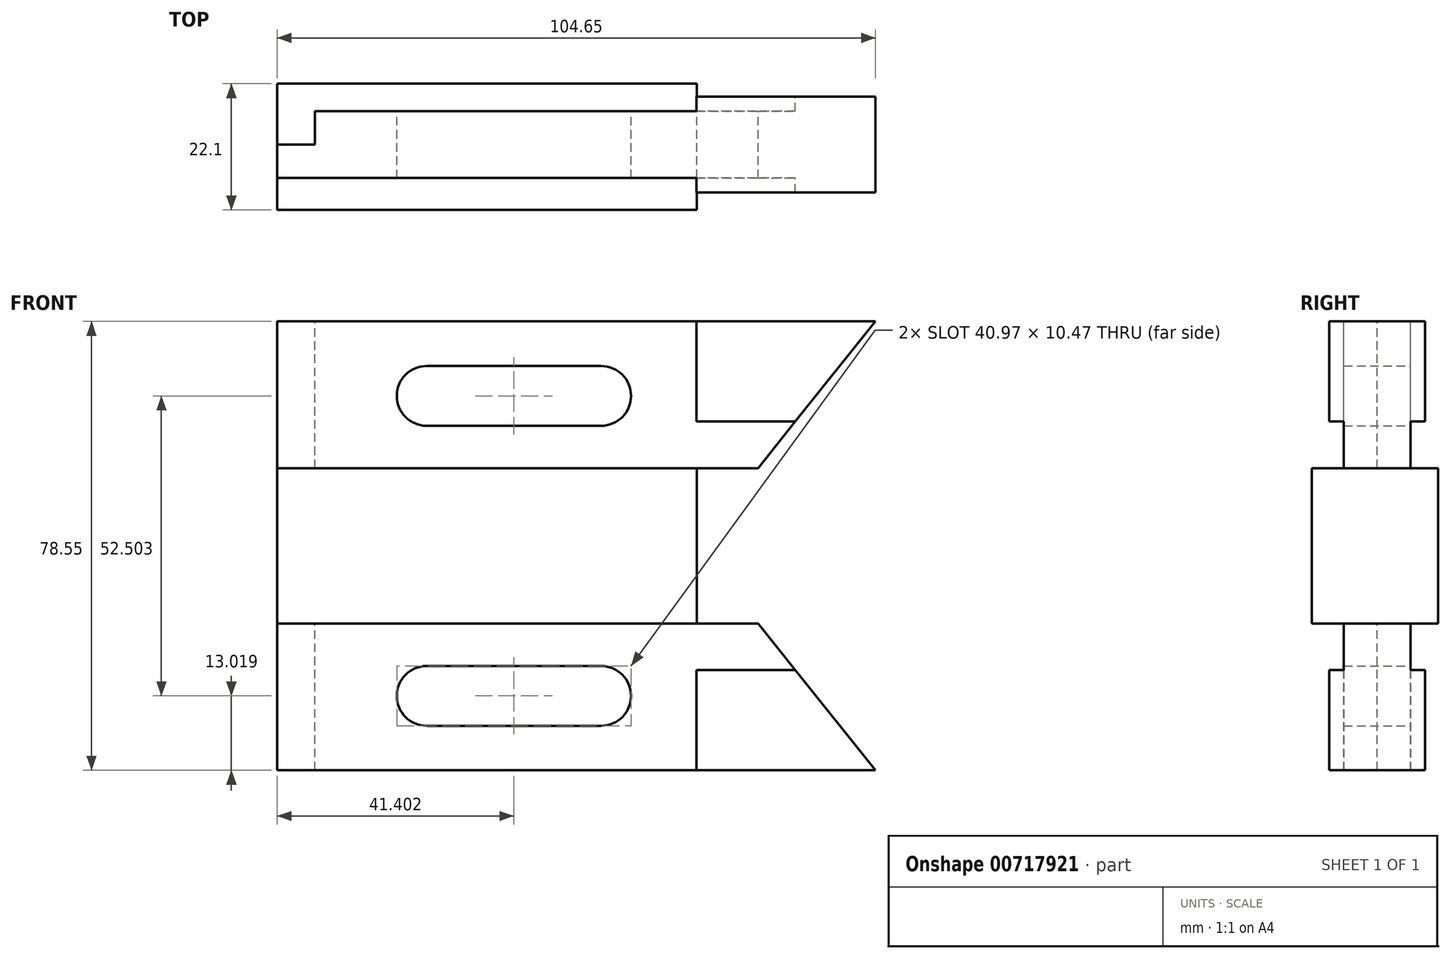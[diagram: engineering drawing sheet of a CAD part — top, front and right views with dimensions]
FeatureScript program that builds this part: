
annotation { "Feature Type Name" : "Feature", "Feature Type Description" : "" }
export const myFeature = defineFeature(function(context is Context, id is Id, definition is map)
    precondition{}
    {
        {
            var Q0;
            Q0=qCreatedBy(makeId("Front.planeOp"),FACE);
            var sketch = newSketch(context, id + "F0", { "sketchPlane" : qUnion([Q0])});
            skLineSegment(sketch, "E0", {"start": v(35.4, 0) * mm, "end": v(-38, 0) * mm});
            skLineSegment(sketch, "E1", {"start": v(-38, 10.01) * mm, "end": v(-38, 18.12) * mm});
            skLineSegment(sketch, "E2", {"start": v(-38, 0) * mm, "end": v(-38, 27.2) * mm});
            skLineSegment(sketch, "E3", {"start": v(-38, 27.2) * mm, "end": v(35.4, 27.2) * mm});
            skLineSegment(sketch, "E4", {"start": v(35.4, 27.2) * mm, "end": v(35.4, 0) * mm});
            skSolve(sketch);
        }
        {
            var Q0;
            {var subQ0=sQuery(id+"F0.wireOp",EDGE,"E0");Q0=makeQuery(id+"F0.imprint","IMPRINT",FACE,{"disambiguationData":[TD([[makeQuery(id+"F0.imprint","IMPRINT",EDGE,{"derivedFrom":subQ0}),-1.0]])]});}
            extrude(context, id + "F1", {"entities" : qUnion([Q0]), "depth" : 22.1 * mm, "offsetDistance" : 25.4 * mm});
        }
        {
            var Q0;
            Q0=qCreatedBy(makeId("Front.planeOp"),FACE);
            cPlane(context, id + "F2", {"entities" : qUnion([Q0]), "cplaneType" : CPlaneType.OFFSET, "offset" : 10.67 * mm, "width" : 152.4 * mm, "height" : 152.4 * mm});
        }
        {
            var Q0;
            Q0=qCreatedBy(id+"F2.planeOp",FACE);
            var sketch = newSketch(context, id + "F3", { "sketchPlane" : qUnion([Q0])});
            skLineSegment(sketch, "E5", {"start": v(-38, 27.2) * mm, "end": v(46.1, 27.2) * mm});
            skLineSegment(sketch, "E6", {"start": v(46.1, 27.2) * mm, "end": v(66.64, 52.87) * mm});
            skLineSegment(sketch, "E7", {"start": v(-38, 27.2) * mm, "end": v(-38, 52.87) * mm});
            skLineSegment(sketch, "E8", {"start": v(-38, 52.87) * mm, "end": v(66.64, 52.87) * mm});
            skLineSegment(sketch, "E9", {"start": v(-38, 0) * mm, "end": v(46.1, 0) * mm});
            skLineSegment(sketch, "E10", {"start": v(46.1, 0) * mm, "end": v(66.64, -25.68) * mm});
            skLineSegment(sketch, "E11", {"start": v(66.64, -25.68) * mm, "end": v(-38, -25.68) * mm});
            skLineSegment(sketch, "E12", {"start": v(-38, -25.68) * mm, "end": v(-38, 0) * mm});
            skLineSegment(sketch, "E13", {"start": v(-31.41, -25.68) * mm, "end": v(-31.41, 0) * mm});
            skLineSegment(sketch, "E14", {"start": v(-31.41, 0) * mm, "end": v(35.33, 0) * mm});
            skLineSegment(sketch, "E15", {"start": v(35.33, 0) * mm, "end": v(46.1, 0) * mm});
            skLineSegment(sketch, "E16", {"start": v(52.62, -8.15) * mm, "end": v(35.33, -8.15) * mm});
            skLineSegment(sketch, "E17", {"start": v(35.33, -8.15) * mm, "end": v(35.33, -25.68) * mm});
            skLineSegment(sketch, "E18", {"start": v(52.62, 35.34) * mm, "end": v(35.33, 35.34) * mm});
            skLineSegment(sketch, "E19", {"start": v(35.33, 35.34) * mm, "end": v(35.33, 52.87) * mm});
            skLineSegment(sketch, "E20", {"start": v(-31.41, 27.2) * mm, "end": v(-31.41, 52.87) * mm});
            skLineSegment(sketch, "E21", {"start": v(-11.86, -17.9) * mm, "end": v(18.64, -17.9) * mm});
            skArc(sketch, "E22", {"start": v(18.64, -17.9) * mm, "mid": v(23.88, -12.66) * mm, "end": v(18.64, -7.43) * mm});
            skLineSegment(sketch, "E23", {"start": v(18.64, -7.43) * mm, "end": v(-11.86, -7.43) * mm});
            skArc(sketch, "E24", {"start": v(-11.86, -7.43) * mm, "mid": v(-17.1, -12.66) * mm, "end": v(-11.86, -17.9) * mm});
            skLineSegment(sketch, "E25", {"start": v(18.64, 34.6) * mm, "end": v(-11.86, 34.6) * mm});
            skArc(sketch, "E26", {"start": v(18.64, 34.6) * mm, "mid": v(23.88, 39.84) * mm, "end": v(18.64, 45.08) * mm});
            skLineSegment(sketch, "E27", {"start": v(18.64, 45.08) * mm, "end": v(-11.86, 45.08) * mm});
            skArc(sketch, "E28", {"start": v(-11.86, 45.08) * mm, "mid": v(-17.1, 39.84) * mm, "end": v(-11.86, 34.6) * mm});
            skSolve(sketch);
        }
        {
            var Q0;
            {var subQ1=sQuery(id+"F3.wireOp",EDGE,"E13");Q0=makeQuery(id+"F3.imprint","IMPRINT",FACE,{"disambiguationData":[TD([[makeQuery(id+"F3.imprint","IMPRINT",EDGE,{"derivedFrom":subQ1}),-1.0]])]});}
            var Q1;
            {var subQ0=sQuery(id+"F3.wireOp",EDGE,"E18");Q1=makeQuery(id+"F3.imprint","IMPRINT",FACE,{"disambiguationData":[TD([[makeQuery(id+"F3.imprint","IMPRINT",EDGE,{"derivedFrom":subQ0}),1.0]])]});}
            extrude(context, id + "F4", {"entities" : qUnion([Q0, Q1]), "operationType" : NewBodyOperationType.ADD, "endBound" : BoundingType.SYMMETRIC, "depth" : 11.68 * mm, "offsetDistance" : 25.4 * mm});
        }
        {
            var Q0;
            {var subQ0=sQuery(id+"F3.wireOp",EDGE,"E16");Q0=makeQuery(id+"F3.imprint","IMPRINT",FACE,{"disambiguationData":[TD([[makeQuery(id+"F3.imprint","IMPRINT",EDGE,{"derivedFrom":subQ0}),1.0]])]});}
            var Q1;
            {var subQ0=sQuery(id+"F3.wireOp",EDGE,"E18");Q1=makeQuery(id+"F3.imprint","IMPRINT",FACE,{"disambiguationData":[TD([[makeQuery(id+"F3.imprint","IMPRINT",EDGE,{"derivedFrom":subQ0}),-1.0]])]});}
            extrude(context, id + "F5", {"entities" : qUnion([Q0, Q1]), "operationType" : NewBodyOperationType.ADD, "endBound" : BoundingType.SYMMETRIC, "depth" : 16.76 * mm, "offsetDistance" : 25.4 * mm});
        }
        {
            var Q0;
            {var subQ2=sQuery(id+"F3.wireOp",EDGE,"E12");Q0=makeQuery(id+"F3.imprint","IMPRINT",FACE,{"disambiguationData":[TD([[makeQuery(id+"F3.imprint","IMPRINT",EDGE,{"derivedFrom":subQ2}),-1.0]])]});}
            var Q1;
            Q1=makeQuery(id+"F4.opExtrude","CAP_FACE",FACE,{"disambiguationData":[OSD([sQuery(id+"F3.wireOp",EDGE,"E9"),sQuery(id+"F3.wireOp",EDGE,"E10"),sQuery(id+"F3.wireOp",EDGE,"E11"),sQuery(id+"F3.wireOp",EDGE,"E13"),sQuery(id+"F3.wireOp",EDGE,"E16"),sQuery(id+"F3.wireOp",EDGE,"E17"),sQuery(id+"F3.wireOp",EDGE,"E21"),sQuery(id+"F3.wireOp",EDGE,"E22"),sQuery(id+"F3.wireOp",EDGE,"E23"),sQuery(id+"F3.wireOp",EDGE,"E24")])],"isStart":false});
            extrude(context, id + "F6", {"entities" : qUnion([Q0]), "operationType" : NewBodyOperationType.ADD, "endBound" : BoundingType.UP_TO_SURFACE, "depth" : 25.4 * mm, "endBoundEntityFace" : qUnion([Q1]), "offsetDistance" : 25.4 * mm});
        }
        {
            var Q0;
            {var subQ2=sQuery(id+"F3.wireOp",EDGE,"E7");Q0=makeQuery(id+"F3.imprint","IMPRINT",FACE,{"disambiguationData":[TD([[makeQuery(id+"F3.imprint","IMPRINT",EDGE,{"derivedFrom":subQ2}),-1.0]])]});}
            var Q1;
            Q1=makeQuery(id+"F4.opExtrude","CAP_FACE",FACE,{"disambiguationData":[OSD([sQuery(id+"F3.wireOp",EDGE,"E5"),sQuery(id+"F3.wireOp",EDGE,"E6"),sQuery(id+"F3.wireOp",EDGE,"E8"),sQuery(id+"F3.wireOp",EDGE,"E18"),sQuery(id+"F3.wireOp",EDGE,"E19"),sQuery(id+"F3.wireOp",EDGE,"E20"),sQuery(id+"F3.wireOp",EDGE,"E25"),sQuery(id+"F3.wireOp",EDGE,"E26"),sQuery(id+"F3.wireOp",EDGE,"E27"),sQuery(id+"F3.wireOp",EDGE,"E28")])],"isStart":false});
            extrude(context, id + "F7", {"entities" : qUnion([Q0]), "operationType" : NewBodyOperationType.ADD, "endBound" : BoundingType.UP_TO_SURFACE, "depth" : 25.4 * mm, "endBoundEntityFace" : qUnion([Q1]), "offsetDistance" : 25.4 * mm});
        }
    });
